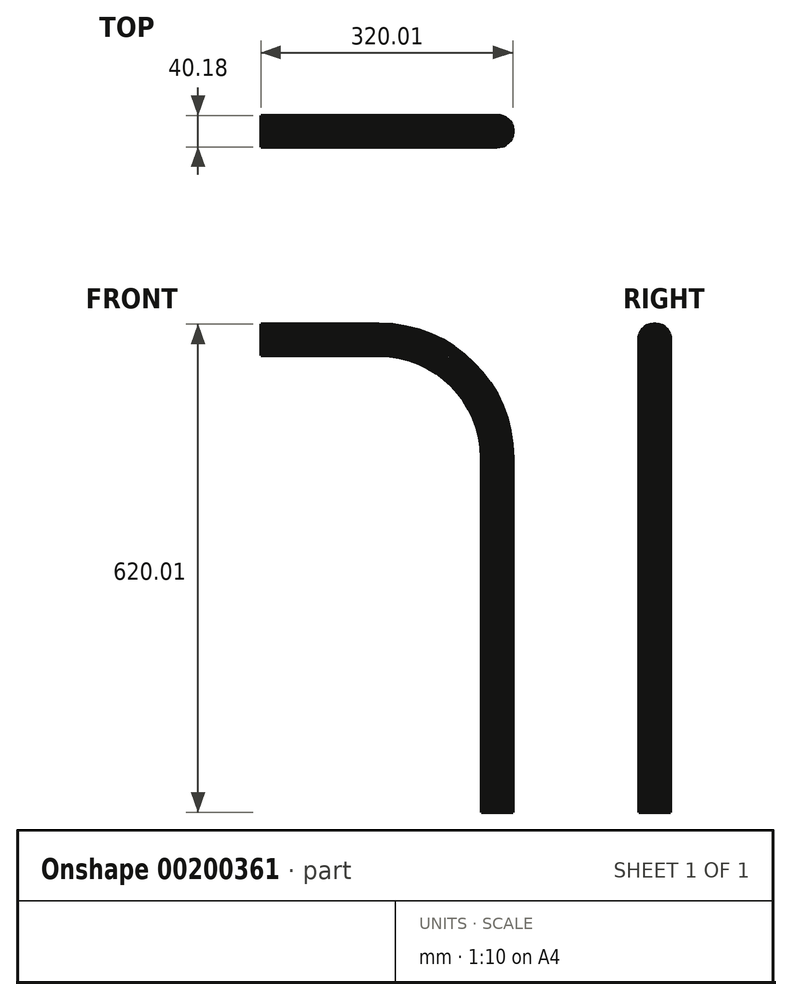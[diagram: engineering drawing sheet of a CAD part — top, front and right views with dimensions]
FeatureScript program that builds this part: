
annotation { "Feature Type Name" : "Feature", "Feature Type Description" : "" }
export const myFeature = defineFeature(function(context is Context, id is Id, definition is map)
    precondition{}
    {
        {
            var Q0;
            Q0=qCreatedBy(makeId("Top.planeOp"),FACE);
            var sketch = newSketch(context, id + "F0", { "sketchPlane" : qUnion([Q0])});
            skCircle(sketch, "E0.cCircle", {"center": v(0, 0) * mm, "radius": 20 * mm, "construction": true});
            skLineSegment(sketch, "E0.0", {"start": v(-19.3, -5.57) * mm, "end": v(-20, -1.93) * mm});
            skLineSegment(sketch, "E0.1", {"start": v(-20, -1.93) * mm, "end": v(-20, 1.78) * mm});
            skLineSegment(sketch, "E0.2", {"start": v(-20, 1.78) * mm, "end": v(-19.34, 5.43) * mm});
            skLineSegment(sketch, "E0.3", {"start": v(-19.34, 5.43) * mm, "end": v(-18.01, 8.89) * mm});
            skLineSegment(sketch, "E0.4", {"start": v(-18.01, 8.89) * mm, "end": v(-16.07, 12.05) * mm});
            skLineSegment(sketch, "E0.5", {"start": v(-16.07, 12.05) * mm, "end": v(-13.59, 14.8) * mm});
            skLineSegment(sketch, "E0.6", {"start": v(-13.59, 14.8) * mm, "end": v(-10.64, 17.04) * mm});
            skLineSegment(sketch, "E0.7", {"start": v(-10.64, 17.04) * mm, "end": v(-7.32, 18.7) * mm});
            skLineSegment(sketch, "E0.8", {"start": v(-7.32, 18.7) * mm, "end": v(-3.76, 19.73) * mm});
            skLineSegment(sketch, "E0.9", {"start": v(-3.76, 19.73) * mm, "end": v(-0.07, 20.09) * mm});
            skLineSegment(sketch, "E0.10", {"start": v(-0.07, 20.09) * mm, "end": v(3.62, 19.76) * mm});
            skLineSegment(sketch, "E0.11", {"start": v(3.62, 19.76) * mm, "end": v(7.19, 18.76) * mm});
            skLineSegment(sketch, "E0.12", {"start": v(7.19, 18.76) * mm, "end": v(10.51, 17.12) * mm});
            skLineSegment(sketch, "E0.13", {"start": v(10.51, 17.12) * mm, "end": v(13.48, 14.9) * mm});
            skLineSegment(sketch, "E0.14", {"start": v(13.48, 14.9) * mm, "end": v(15.98, 12.16) * mm});
            skLineSegment(sketch, "E0.15", {"start": v(15.98, 12.16) * mm, "end": v(17.95, 9.02) * mm});
            skLineSegment(sketch, "E0.16", {"start": v(17.95, 9.02) * mm, "end": v(19.3, 5.57) * mm});
            skLineSegment(sketch, "E0.17", {"start": v(19.3, 5.57) * mm, "end": v(20, 1.93) * mm});
            skLineSegment(sketch, "E0.18", {"start": v(20, 1.93) * mm, "end": v(20, -1.78) * mm});
            skLineSegment(sketch, "E0.19", {"start": v(20, -1.78) * mm, "end": v(19.34, -5.43) * mm});
            skLineSegment(sketch, "E0.20", {"start": v(19.34, -5.43) * mm, "end": v(18.01, -8.89) * mm});
            skLineSegment(sketch, "E0.21", {"start": v(18.01, -8.89) * mm, "end": v(16.07, -12.05) * mm});
            skLineSegment(sketch, "E0.22", {"start": v(16.07, -12.05) * mm, "end": v(13.59, -14.8) * mm});
            skLineSegment(sketch, "E0.23", {"start": v(13.59, -14.8) * mm, "end": v(10.64, -17.04) * mm});
            skLineSegment(sketch, "E0.24", {"start": v(10.64, -17.04) * mm, "end": v(7.32, -18.7) * mm});
            skLineSegment(sketch, "E0.25", {"start": v(7.32, -18.7) * mm, "end": v(3.76, -19.73) * mm});
            skLineSegment(sketch, "E0.26", {"start": v(3.76, -19.73) * mm, "end": v(0.07, -20.09) * mm});
            skLineSegment(sketch, "E0.27", {"start": v(0.07, -20.09) * mm, "end": v(-3.62, -19.76) * mm});
            skLineSegment(sketch, "E0.28", {"start": v(-3.62, -19.76) * mm, "end": v(-7.19, -18.76) * mm});
            skLineSegment(sketch, "E0.29", {"start": v(-7.19, -18.76) * mm, "end": v(-10.51, -17.12) * mm});
            skLineSegment(sketch, "E0.30", {"start": v(-10.51, -17.12) * mm, "end": v(-13.48, -14.9) * mm});
            skLineSegment(sketch, "E0.31", {"start": v(-13.48, -14.9) * mm, "end": v(-15.98, -12.16) * mm});
            skLineSegment(sketch, "E0.32", {"start": v(-15.98, -12.16) * mm, "end": v(-17.95, -9.02) * mm});
            skLineSegment(sketch, "E0.33", {"start": v(-17.95, -9.02) * mm, "end": v(-19.3, -5.57) * mm});
            skPoint(sketch, "E0.0.midPoint", {"position": v(-19.65, -3.75) * mm});
            skSolve(sketch);
        }
        {
            var Q0;
            Q0=qCreatedBy(makeId("Front.planeOp"),FACE);
            var sketch = newSketch(context, id + "F1", { "sketchPlane" : qUnion([Q0])});
            skLineSegment(sketch, "E1", {"start": v(0, 0) * mm, "end": v(0, 450) * mm});
            skArc(sketch, "E2", {"start": v(0, 450) * mm, "mid": v(-43.93, 556.07) * mm, "end": v(-150, 600) * mm});
            skLineSegment(sketch, "E3", {"start": v(-150, 600) * mm, "end": v(-300, 600) * mm});
            skSolve(sketch);
        }
        {
            var Q0;
            Q0 = qSketchRegion(id + "F0", true);
            var Q1;
            Q1=sQuery(id+"F1.wireOp",EDGE,"E1");
            var Q2;
            Q2=sQuery(id+"F1.wireOp",EDGE,"E2");
            var Q3;
            Q3=sQuery(id+"F1.wireOp",EDGE,"E3");
            sweep(context, id + "F2", {"profiles" : qUnion([Q0]), "path" : qUnion([Q1, Q2, Q3])});
        }
    });
